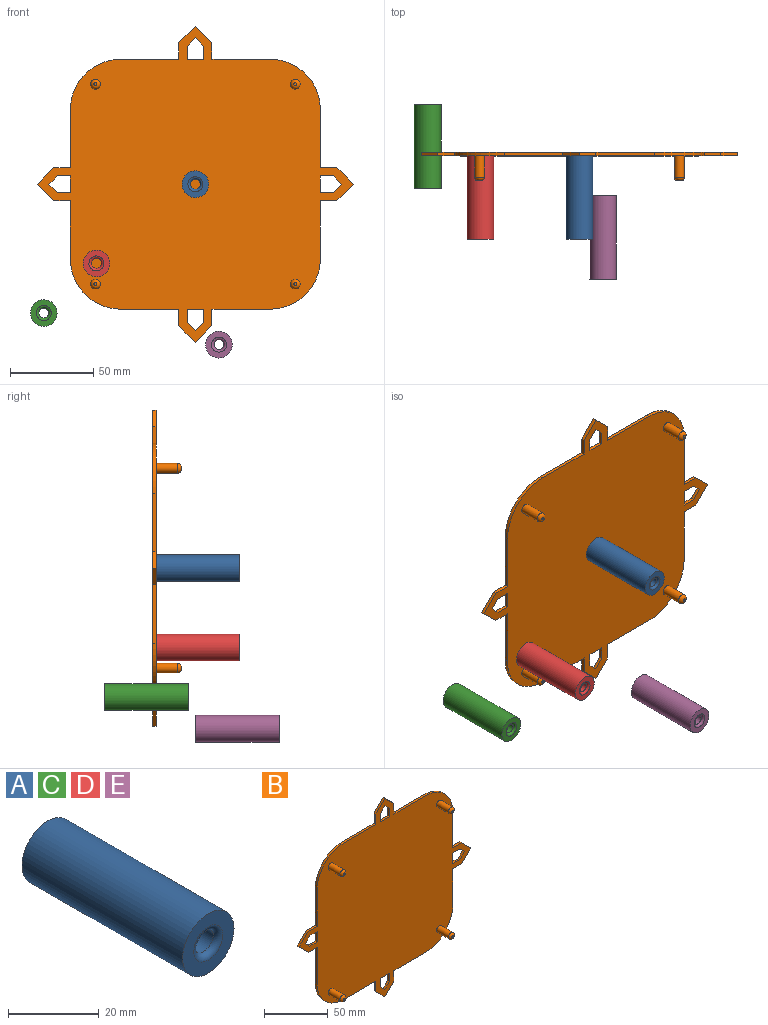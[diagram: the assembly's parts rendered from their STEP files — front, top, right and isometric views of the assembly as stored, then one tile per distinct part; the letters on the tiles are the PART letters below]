
ASSEMBLY  parts=5 mates=2
PART A: 6 faces, bbox 16x50x16 mm
  f0: cylinder r=3mm len=47mm, axis (0,1,0), area 885.9mm2, adj f4,f5
  f1: cylinder r=8mm len=50mm, axis (0,1,0), area 2513.3mm2, adj f2,f3
  f2: plane 16x16mm, normal (0,-1,0), area 137.4mm2, adj f1,f4
  f3: plane 16x16mm, normal (0,1,0), area 137.4mm2, adj f1,f5
  f4: torus R=4.5mm, axis (0,-1,0), area 52.5mm2, adj f0,f2
  f5: torus R=4.5mm, axis (0,-1,0), area 52.5mm2, adj f0,f3
PART B: 62 faces, bbox 190x17x190 mm
  f0: plane 35x2mm, normal (0,0,-1), area 70mm2, adj f4,f5,f6,f33
  f1: plane 35x2mm, normal (1,0,0), area 70mm2, adj f4,f5,f7,f33
  f2: plane 35x2mm, normal (0,0,1), area 70mm2, adj f4,f5,f12,f31
  f3: plane 35x2mm, normal (-1,0,0), area 70mm2, adj f4,f5,f21,f32
  f4: plane 190x190mm, normal (0,-1,0), area 22404.6mm2, adj f0,f1,f2,f3,f6,f7,f8,f9
  f5: plane 190x190mm, normal (0,1,0), area 22510.3mm2, adj f0,f1,f2,f3,f6,f7,f8,f9
  f6: plane 10x2mm, normal (1,0,0), area 20mm2, adj f0,f4,f5,f25
  f7: plane 10x2mm, normal (0,0,-1), area 20mm2, adj f1,f4,f5,f8
  f8: plane 10x10mm, normal (0.71,0,-0.71), area 28.3mm2, adj f4,f5,f7,f9
  f9: plane 10x10mm, normal (0.71,0,0.71), area 28.3mm2, adj f4,f5,f8,f10
  f10: plane 10x2mm, normal (0,0,1), area 20mm2, adj f4,f5,f9,f11
  f11: plane 35x2mm, normal (1,0,0), area 70mm2, adj f4,f5,f10,f31
  f12: plane 10x2mm, normal (1,0,0), area 20mm2, adj f2,f4,f5,f13
  f13: plane 10x10mm, normal (0.71,0,0.71), area 28.3mm2, adj f4,f5,f12,f14
  f14: plane 10x10mm, normal (-0.71,0,0.71), area 28.3mm2, adj f4,f5,f13,f15
  f15: plane 10x2mm, normal (-1,0,0), area 20mm2, adj f4,f5,f14,f16
  f16: plane 35x2mm, normal (0,0,1), area 70mm2, adj f4,f5,f15,f34
  f17: plane 35x2mm, normal (-1,0,0), area 70mm2, adj f4,f5,f18,f34
  f18: plane 10x2mm, normal (0,0,1), area 20mm2, adj f4,f5,f17,f19
  f19: plane 10x10mm, normal (-0.71,0,0.71), area 28.3mm2, adj f4,f5,f18,f20
  f20: plane 10x10mm, normal (-0.71,0,-0.71), area 28.3mm2, adj f4,f5,f19,f21
  f21: plane 10x2mm, normal (0,0,-1), area 20mm2, adj f3,f4,f5,f20
  f22: plane 35x2mm, normal (0,0,-1), area 70mm2, adj f4,f5,f23,f32
  f23: plane 10x2mm, normal (-1,0,0), area 20mm2, adj f4,f5,f22,f24
  f24: plane 10x10mm, normal (-0.71,0,-0.71), area 28.3mm2, adj f4,f5,f23,f25
  f25: plane 10x10mm, normal (0.71,0,-0.71), area 28.3mm2, adj f4,f5,f6,f24
  f26: plane 5x5mm, normal (0.71,0,0.71), area 14.1mm2, adj f4,f5,f27,f30
  f27: plane 7.93x2mm, normal (0,0,1), area 15.9mm2, adj f4,f5,f26,f28
  f28: plane 10x2mm, normal (-1,0,0), area 20mm2, adj f4,f5,f27,f29
  f29: plane 7.93x2mm, normal (0,0,-1), area 15.9mm2, adj f4,f5,f28,f30
  f30: plane 5x5mm, normal (0.71,0,-0.71), area 14.1mm2, adj f4,f5,f26,f29
  f31: cylinder r=30mm len=30mm, axis (0,-1,0), area 94.2mm2, adj f2,f4,f5,f11
  f32: cylinder r=30mm len=30mm, axis (0,-1,0), area 94.2mm2, adj f3,f4,f5,f22
  f33: cylinder r=30mm len=30mm, axis (0,-1,0), area 94.2mm2, adj f0,f1,f4,f5
  f34: cylinder r=30mm len=30mm, axis (0,-1,0), area 94.2mm2, adj f4,f5,f16,f17
  f35: plane 7.93x2mm, normal (-1,0,0), area 15.9mm2, adj f4,f5,f36,f39
  f36: plane 5x5mm, normal (-0.71,0,-0.71), area 14.1mm2, adj f4,f5,f35,f37
  f37: plane 5x5mm, normal (0.71,0,-0.71), area 14.1mm2, adj f4,f5,f36,f38
  f38: plane 7.93x2mm, normal (1,0,0), area 15.9mm2, adj f4,f5,f37,f39
  f39: plane 10x2mm, normal (0,0,1), area 20mm2, adj f4,f5,f35,f38
  f40: plane 7.93x2mm, normal (0,0,1), area 15.9mm2, adj f4,f5,f41,f44
  f41: plane 5x5mm, normal (-0.71,0,0.71), area 14.1mm2, adj f4,f5,f40,f42
  f42: plane 5x5mm, normal (-0.71,0,-0.71), area 14.1mm2, adj f4,f5,f41,f43
  f43: plane 7.93x2mm, normal (0,0,-1), area 15.9mm2, adj f4,f5,f42,f44
  f44: plane 10x2mm, normal (1,0,0), area 20mm2, adj f4,f5,f40,f43
  f45: plane 5x5mm, normal (-0.71,0,0.71), area 14.1mm2, adj f4,f5,f46,f49
  f46: plane 7.93x2mm, normal (-1,0,0), area 15.9mm2, adj f4,f5,f45,f47
  f47: plane 10x2mm, normal (0,0,-1), area 20mm2, adj f4,f5,f46,f48
  f48: plane 7.93x2mm, normal (1,0,0), area 15.9mm2, adj f4,f5,f47,f49
  f49: plane 5x5mm, normal (0.71,0,0.71), area 14.1mm2, adj f4,f5,f45,f48
  f50: cylinder r=2.9mm len=13mm, axis (0,1,0), area 236.9mm2, adj f4,f61
  f51: plane 1.8x1.8mm, normal (0,-1,0), area 2.5mm2, adj f61
  f52: cylinder r=2.9mm len=13mm, axis (0,1,0), area 236.9mm2, adj f4,f60
  f53: plane 1.8x1.8mm, normal (0,-1,0), area 2.5mm2, adj f60
  f54: cylinder r=2.9mm len=13mm, axis (0,1,0), area 236.9mm2, adj f4,f59
  f55: plane 1.8x1.8mm, normal (0,-1,0), area 2.5mm2, adj f59
  f56: cylinder r=2.9mm len=13mm, axis (0,1,0), area 236.9mm2, adj f4,f58
  f57: plane 1.8x1.8mm, normal (0,-1,0), area 2.5mm2, adj f58
  f58: torus R=0.9mm, axis (0,-1,0), area 42.9mm2, adj f56,f57
  f59: torus R=0.9mm, axis (0,-1,0), area 42.9mm2, adj f54,f55
  f60: torus R=0.9mm, axis (0,-1,0), area 42.9mm2, adj f52,f53
  f61: torus R=0.9mm, axis (0,-1,0), area 42.9mm2, adj f50,f51
PART C: same geometry as A
PART D: same geometry as A
PART E: same geometry as A
PLACE A t=(-99.92,-120.98,69.85)mm
PLACE B t=(-24.92,-118.98,-5.15)mm
PLACE C t=(-190.94,-90.25,-7.52)mm
PLACE D t=(-159.31,-120.98,22.28)mm
PLACE E t=(-85.71,-144.83,-26.5)mm
MATE planar B.f32 <-> D.f0  axis (0,-1,0) through (-144.92,-120.98,24.85)mm
MATE planar B.f4 <-> A.f0  axis (0,-1,0) through (-99.92,-120.98,69.85)mm
